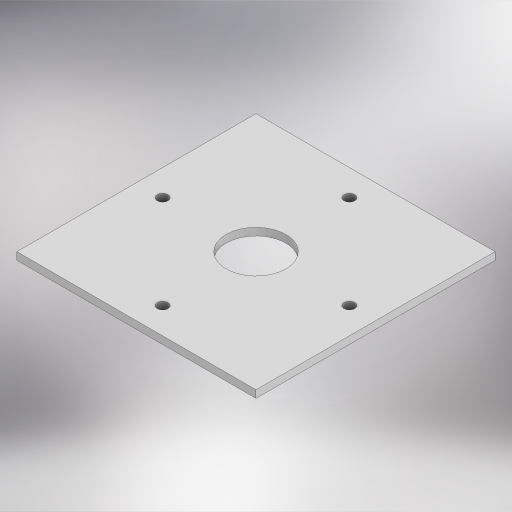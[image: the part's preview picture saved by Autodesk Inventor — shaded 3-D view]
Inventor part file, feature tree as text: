
AUTODESK INVENTOR PART (.ipt)
format: ipt  version: 2024 (Build 280153000, 153)  size: 279,040 bytes
history: native  units: in
note: dims shown in document units (in); Inventor stores cm internally (conversion verified against a paired STEP export)
features: extrude x1, sketch x1
ambient origin geometry x8: Origin, YZ Plane, XZ Plane, XY Plane, X Axis, Y Axis, Z Axis, Center Point
bodies: Solid1 (feature_tree)
feature tree (2):
  extrude  "Extrusion1"  Depth=4.0in
  sketch  "Sketch1"  dims[d0=4.0in d1=4.0in d2=0.18in d3=0.4375in d4=1.0in d5=1.5748in d7=360.0deg d9=0.125in d10=0.0in]
